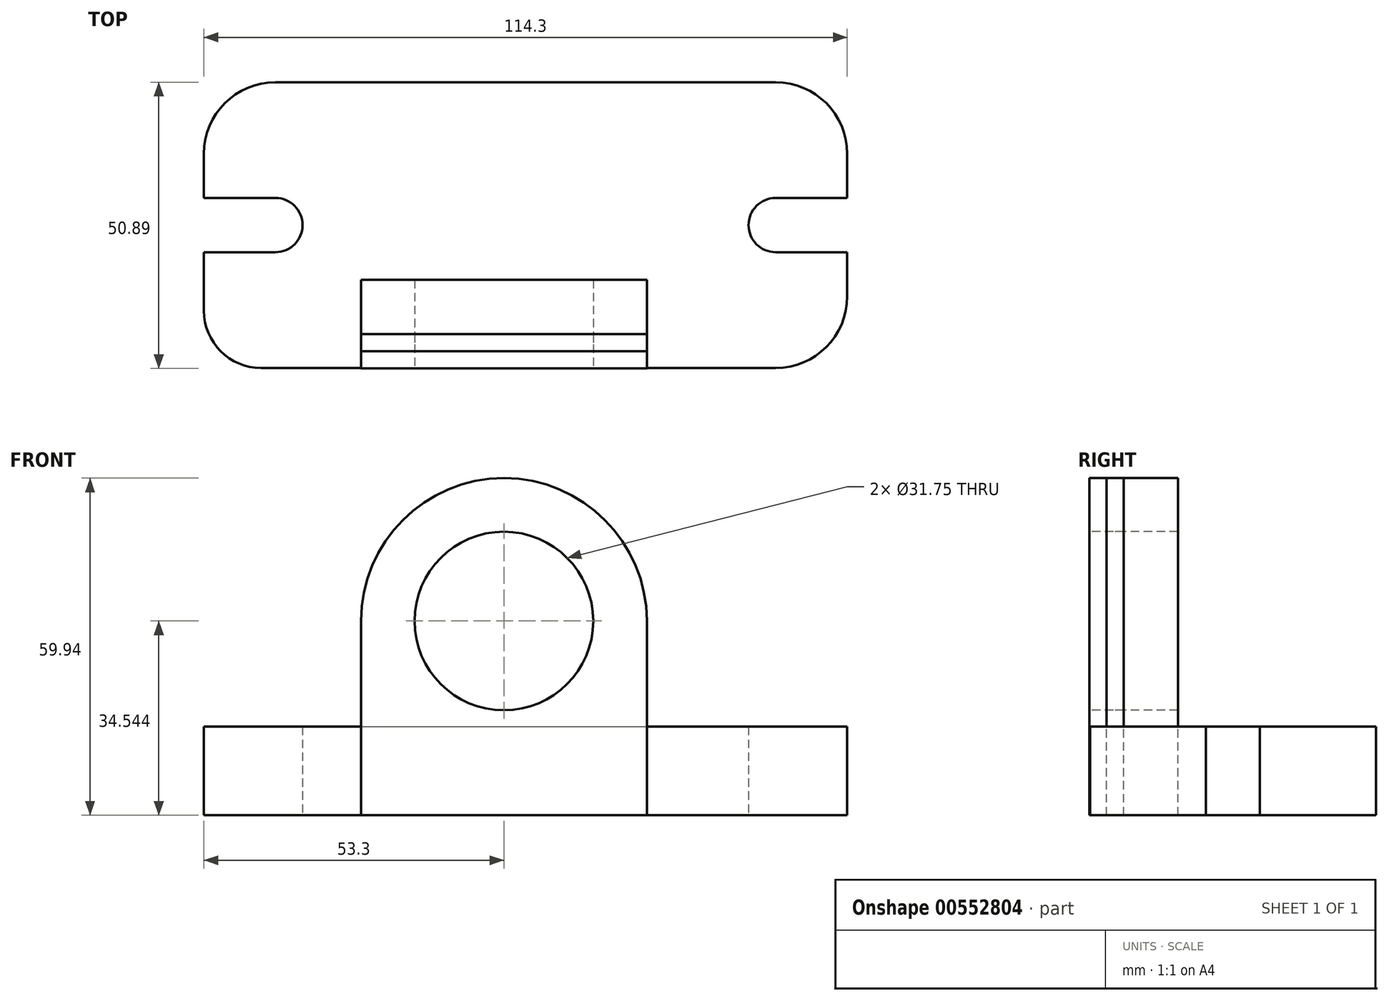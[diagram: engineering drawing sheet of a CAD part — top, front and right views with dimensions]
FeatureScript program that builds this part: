
annotation { "Feature Type Name" : "Feature", "Feature Type Description" : "" }
export const myFeature = defineFeature(function(context is Context, id is Id, definition is map)
    precondition{}
    {
        {
            var Q0;
            Q0=qCreatedBy(makeId("Top.planeOp"),FACE);
            var sketch = newSketch(context, id + "F0", { "sketchPlane" : qUnion([Q0])});
            skLineSegment(sketch, "E0.bottom", {"start": v(-43.14, 0.1) * mm, "end": v(48.3, 0.1) * mm});
            skLineSegment(sketch, "E0.top", {"start": v(-40.6, 50.9) * mm, "end": v(48.3, 50.9) * mm});
            skLineSegment(sketch, "E0.left", {"start": v(-53.3, 10.25) * mm, "end": v(-53.3, 38.2) * mm});
            skLineSegment(sketch, "E0.right", {"start": v(61, 12.8) * mm, "end": v(61, 38.2) * mm});
            skPoint(sketch, "E1.visualSharp", {"position": v(-53.3, 0.1) * mm});
            skArc(sketch, "E1.filletArc", {"start": v(-53.3, 10.25) * mm, "mid": v(-50.33, 3.07) * mm, "end": v(-43.14, 0.1) * mm});
            skPoint(sketch, "E2.visualSharp", {"position": v(61, 0.1) * mm});
            skArc(sketch, "E2.filletArc", {"start": v(48.3, 0.1) * mm, "mid": v(57.28, 3.81) * mm, "end": v(61, 12.8) * mm});
            skPoint(sketch, "E3.visualSharp", {"position": v(61, 50.9) * mm});
            skArc(sketch, "E3.filletArc", {"start": v(61, 38.2) * mm, "mid": v(57.28, 47.17) * mm, "end": v(48.3, 50.9) * mm});
            skPoint(sketch, "E4.visualSharp", {"position": v(-53.3, 50.9) * mm});
            skArc(sketch, "E4.filletArc", {"start": v(-40.6, 50.9) * mm, "mid": v(-49.58, 47.17) * mm, "end": v(-53.3, 38.2) * mm});
            skLineSegment(sketch, "E5", {"start": v(-53.3, 20.67) * mm, "end": v(-40.6, 20.67) * mm});
            skLineSegment(sketch, "E6", {"start": v(-40.6, 20.67) * mm, "end": v(-40.6, 30.32) * mm, "construction": true});
            skLineSegment(sketch, "E7", {"start": v(-40.6, 30.32) * mm, "end": v(-53.3, 30.32) * mm});
            skLineSegment(sketch, "E8", {"start": v(-40.6, 25.5) * mm, "end": v(-58.97, 25.5) * mm, "construction": true});
            skLineSegment(sketch, "E9", {"start": v(-58.97, 25.5) * mm, "end": v(-58.97, 0.1) * mm, "construction": true});
            skArc(sketch, "E10", {"start": v(-40.6, 20.67) * mm, "mid": v(-35.78, 25.5) * mm, "end": v(-40.6, 30.32) * mm});
            skLineSegment(sketch, "E11.bottom", {"start": v(61, 20.67) * mm, "end": v(48.3, 20.67) * mm});
            skLineSegment(sketch, "E11.top", {"start": v(61, 30.32) * mm, "end": v(48.3, 30.32) * mm});
            skLineSegment(sketch, "E11.left", {"start": v(61, 20.67) * mm, "end": v(61, 30.32) * mm});
            skLineSegment(sketch, "E11.right", {"start": v(48.3, 20.67) * mm, "end": v(48.3, 30.32) * mm, "construction": true});
            skLineSegment(sketch, "E12", {"start": v(48.3, 25.5) * mm, "end": v(69.2, 25.5) * mm, "construction": true});
            skPoint(sketch, "E12.endSnap0", {"position": v(61, 25.5) * mm});
            skLineSegment(sketch, "E13", {"start": v(69.2, 25.5) * mm, "end": v(69.2, 0.1) * mm, "construction": true});
            skArc(sketch, "E14", {"start": v(48.3, 30.32) * mm, "mid": v(43.47, 25.5) * mm, "end": v(48.3, 20.67) * mm});
            skSolve(sketch);
        }
        {
            var Q0;
            Q0=qCreatedBy(makeId("Front.planeOp"),FACE);
            var sketch = newSketch(context, id + "F1", { "sketchPlane" : qUnion([Q0])});
            skLineSegment(sketch, "E15.bottom", {"start": v(-25.4, 0) * mm, "end": v(25.4, 0) * mm});
            skLineSegment(sketch, "E15.top", {"start": v(-25.4, 34.54) * mm, "end": v(25.4, 34.54) * mm});
            skLineSegment(sketch, "E15.left", {"start": v(-25.4, 0) * mm, "end": v(-25.4, 34.54) * mm});
            skLineSegment(sketch, "E15.right", {"start": v(25.4, 0) * mm, "end": v(25.4, 34.54) * mm});
            skArc(sketch, "E16", {"start": v(25.4, 34.54) * mm, "mid": v(0, 59.94) * mm, "end": v(-25.4, 34.54) * mm});
            skCircle(sketch, "E17", {"center": v(0, 34.54) * mm, "radius": 15.88 * mm});
            skCircle(sketch, "E18", {"center": v(0, 34.54) * mm, "radius": 7.94 * mm});
            skSolve(sketch);
        }
        {
            var Q0;
            Q0=makeQuery(id+"F0.imprint","IMPRINT",FACE,{"disambiguationData":[TD([[makeQuery(id+"F0.imprint","IMPRINT",EDGE,{"derivedFrom":sQuery(id+"F0.wireOp",EDGE,"E0.bottom")}),1.0]])]});
            extrude(context, id + "F2", {"entities" : qUnion([Q0]), "depth" : 15.75 * mm, "offsetDistance" : 25.4 * mm});
        }
        {
            var Q0;
            {var subQ0=sQuery(id+"F1.wireOp",EDGE,"E16");Q0=makeQuery(id+"F1.imprint","IMPRINT",FACE,{"disambiguationData":[TD([[makeQuery(id+"F1.imprint","IMPRINT",EDGE,{"derivedFrom":subQ0}),1.0]])]});}
            var Q1;
            Q1=makeQuery(id+"F1.imprint","IMPRINT",FACE,{"disambiguationData":[TD([[makeQuery(id+"F1.imprint","IMPRINT",EDGE,{"derivedFrom":sQuery(id+"F1.wireOp",EDGE,"E15.bottom")}),1.0]])]});
            extrude(context, id + "F3", {"entities" : qUnion([Q0, Q1]), "depth" : -15.75 * mm, "offsetDistance" : 25.4 * mm});
        }
        {
            var Q0;
            {var subQ0=sQuery(id+"F1.wireOp",EDGE,"E18");var subQ1=sQuery(id+"F1.wireOp",EDGE,"E15.top");var subQ2=makeQuery(id+"F1.imprint","INTERSECT",VERTEX,{"disambiguationData":[OD(0.0)],"derivedFrom":[subQ1,subQ0]});Q0=makeQuery(id+"F1.imprint","IMPRINT",FACE,{"disambiguationData":[TD([[makeQuery(id+"F1.imprint","IMPRINT",EDGE,{"disambiguationData":[TD([[subQ2,-1.0]])],"derivedFrom":subQ1}),-1.0]])]});}
            var Q1;
            {var subQ0=sQuery(id+"F1.wireOp",EDGE,"E18");var subQ1=sQuery(id+"F1.wireOp",EDGE,"E15.top");var subQ2=makeQuery(id+"F1.imprint","INTERSECT",VERTEX,{"disambiguationData":[OD(0.0)],"derivedFrom":[subQ1,subQ0]});Q1=makeQuery(id+"F1.imprint","IMPRINT",FACE,{"disambiguationData":[TD([[makeQuery(id+"F1.imprint","IMPRINT",EDGE,{"disambiguationData":[TD([[subQ2,-1.0]])],"derivedFrom":subQ1}),1.0]])]});}
            extrude(context, id + "F4", {"entities" : qUnion([Q0, Q1]), "depth" : -3.05 * mm, "offsetDistance" : 25.4 * mm});
        }
        {
            var Q0;
            {var subQ0=sQuery(id+"F1.wireOp",EDGE,"E17");var subQ1=sQuery(id+"F1.wireOp",EDGE,"E15.top");var subQ2=makeQuery(id+"F1.imprint","INTERSECT",VERTEX,{"disambiguationData":[OD(0.0)],"derivedFrom":[subQ1,subQ0]});Q0=makeQuery(id+"F1.imprint","IMPRINT",FACE,{"disambiguationData":[TD([[makeQuery(id+"F1.imprint","IMPRINT",EDGE,{"disambiguationData":[TD([[subQ2,-1.0]])],"derivedFrom":subQ1}),1.0]])]});}
            var Q1;
            {var subQ0=sQuery(id+"F1.wireOp",EDGE,"E17");var subQ1=sQuery(id+"F1.wireOp",EDGE,"E15.top");var subQ2=makeQuery(id+"F1.imprint","INTERSECT",VERTEX,{"disambiguationData":[OD(0.0)],"derivedFrom":[subQ1,subQ0]});Q1=makeQuery(id+"F1.imprint","IMPRINT",FACE,{"disambiguationData":[TD([[makeQuery(id+"F1.imprint","IMPRINT",EDGE,{"disambiguationData":[TD([[subQ2,-1.0]])],"derivedFrom":subQ1}),-1.0]])]});}
            extrude(context, id + "F5", {"entities" : qUnion([Q0, Q1]), "depth" : -3.05 * mm, "offsetDistance" : 25.4 * mm});
        }
        {
            var Q0;
            Q0=makeQuery(id+"F4.opExtrude","SWEPT_BODY",BODY,{"disambiguationData":[OSD([sQuery(id+"F1.wireOp",EDGE,"E18")])]});
            var Q1;
            Q1=makeQuery(id+"F5.opExtrude","SWEPT_BODY",BODY,{"disambiguationData":[OSD([sQuery(id+"F1.wireOp",EDGE,"E17"),sQuery(id+"F1.wireOp",EDGE,"E18")])]});
            booleanBodies(context, id + "F6", {"operationType" : BooleanOperationType.SUBTRACTION, "tools" : qUnion([Q0]), "targets" : qUnion([Q1])});
        }
        {
            var Q0;
            Q0=makeQuery(id+"F5.opExtrude","SWEPT_BODY",BODY,{"disambiguationData":[OSD([sQuery(id+"F1.wireOp",EDGE,"E17"),sQuery(id+"F1.wireOp",EDGE,"E18")])]});
            transform(context, id + "F7", {"entities" : qUnion([Q0]), "transformType" : TransformType.TRANSLATION_3D, "dx" : 0 * mm, "dy" : 3.05 * mm, "dz" : 0 * mm, "makeCopy" : false});
        }
    });
